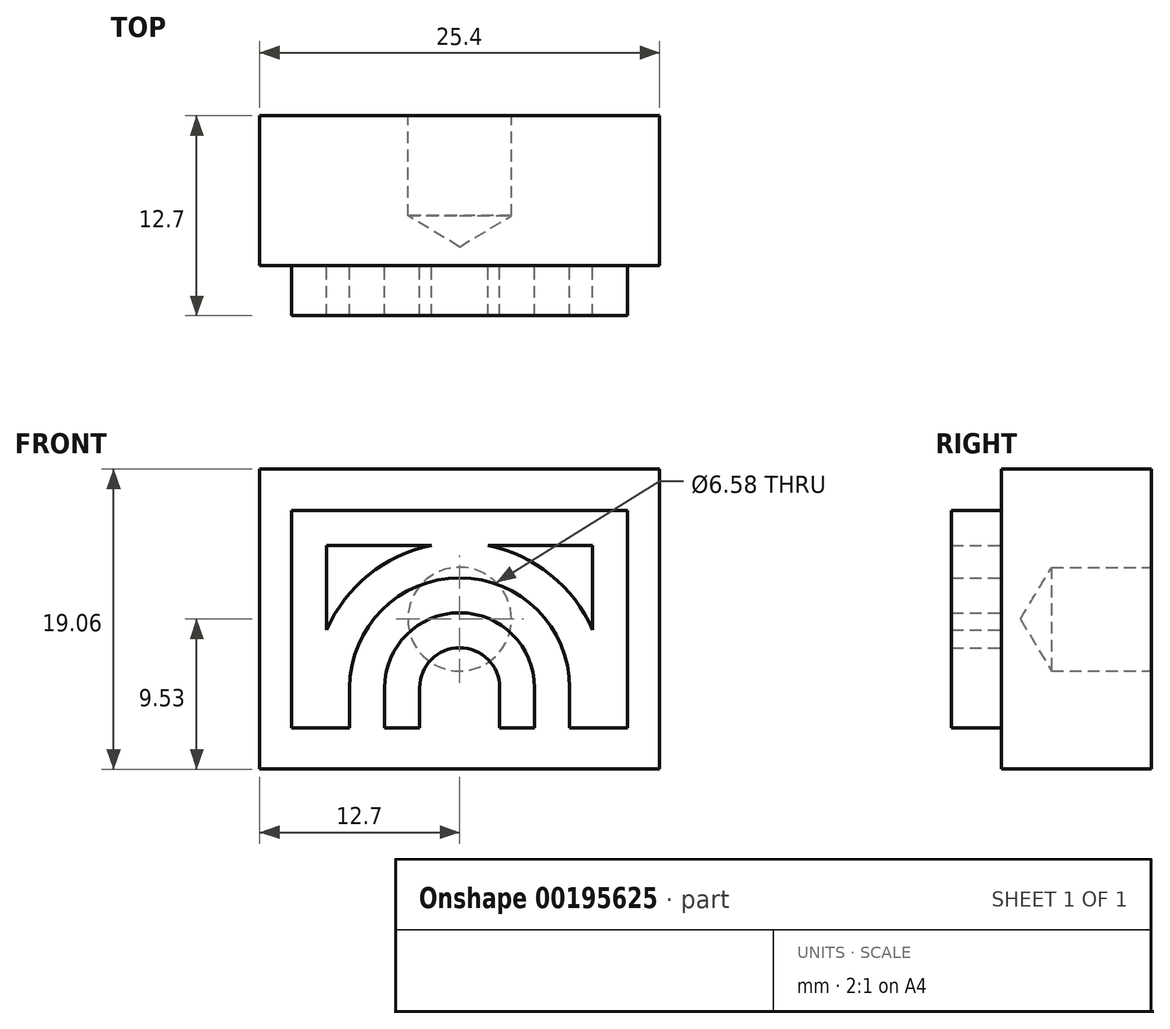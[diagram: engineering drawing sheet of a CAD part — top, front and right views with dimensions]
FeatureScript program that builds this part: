
annotation { "Feature Type Name" : "Feature", "Feature Type Description" : "" }
export const myFeature = defineFeature(function(context is Context, id is Id, definition is map)
    precondition{}
    {
        {
            var Q0;
            Q0=qCreatedBy(makeId("Front.planeOp"),FACE);
            var sketch = newSketch(context, id + "F0", { "sketchPlane" : qUnion([Q0])});
            skLineSegment(sketch, "E0", {"start": v(0, 0) * mm, "end": v(0, 23.02) * mm, "construction": true});
            skLineSegment(sketch, "E1", {"start": v(0, 0) * mm, "end": v(0, -23.52) * mm, "construction": true});
            skLineSegment(sketch, "E2", {"start": v(-25.56, 0) * mm, "end": v(25.9, 0) * mm, "construction": true});
            skLineSegment(sketch, "E3.bottom", {"start": v(-12.7, 9.53) * mm, "end": v(12.7, 9.52) * mm});
            skLineSegment(sketch, "E3.top", {"start": v(-12.7, -9.53) * mm, "end": v(12.7, -9.53) * mm});
            skLineSegment(sketch, "E3.left", {"start": v(-12.7, 9.53) * mm, "end": v(-12.7, -9.53) * mm});
            skLineSegment(sketch, "E3.right", {"start": v(12.7, 9.53) * mm, "end": v(12.7, -9.53) * mm});
            skSolve(sketch);
        }
        {
            var Q0;
            Q0 = qSketchRegion(id + "F0", true);
            extrude(context, id + "F1", {"entities" : qUnion([Q0]), "oppositeDirection" : true, "depth" : 9.52 * mm});
        }
        {
            var Q0;
            Q0=makeQuery(id+"F1.opExtrude","CAP_FACE",FACE,{"disambiguationData":[OSD([sQuery(id+"F0.wireOp",EDGE,"E3.bottom"),sQuery(id+"F0.wireOp",EDGE,"E3.top"),sQuery(id+"F0.wireOp",EDGE,"E3.left"),sQuery(id+"F0.wireOp",EDGE,"E3.right")])],"isStart":true});
            var sketch = newSketch(context, id + "F2", { "sketchPlane" : qUnion([Q0])});
            skLineSegment(sketch, "E4", {"start": v(0, 9) * mm, "end": v(0, -9.1) * mm, "construction": true});
            skLineSegment(sketch, "E5.MirrorCS", {"start": v(0, 6.9) * mm, "end": v(10.66, 6.9) * mm});
            skLineSegment(sketch, "E6.MirrorCS", {"start": v(2.54, -6.9) * mm, "end": v(4.76, -6.9) * mm});
            skLineSegment(sketch, "E7.MirrorCS", {"start": v(6.99, -6.9) * mm, "end": v(10.66, -6.9) * mm});
            skLineSegment(sketch, "E8.MirrorCS", {"start": v(2.54, -4.36) * mm, "end": v(2.54, -6.9) * mm});
            skLineSegment(sketch, "E9.MirrorCS", {"start": v(6.99, -4.36) * mm, "end": v(6.99, -6.9) * mm});
            skLineSegment(sketch, "E10.MirrorCS", {"start": v(10.66, -6.9) * mm, "end": v(10.66, 6.9) * mm});
            skLineSegment(sketch, "E11", {"start": v(1.8, 4.67) * mm, "end": v(8.44, 4.67) * mm});
            skLineSegment(sketch, "E12", {"start": v(8.44, 4.67) * mm, "end": v(8.44, -0.68) * mm});
            skLineSegment(sketch, "E13", {"start": v(4.76, -6.9) * mm, "end": v(4.76, -4.36) * mm});
            skLineSegment(sketch, "E14", {"start": v(10.66, -6.9) * mm, "end": v(0, -6.9) * mm, "construction": true});
            skLineSegment(sketch, "E15", {"start": v(0, -4.36) * mm, "end": v(10.66, -4.36) * mm, "construction": true});
            skArc(sketch, "E16", {"start": v(2.54, -4.36) * mm, "mid": v(1.8, -2.56) * mm, "end": v(0, -1.82) * mm});
            skArc(sketch, "E17", {"start": v(6.99, -4.36) * mm, "mid": v(4.94, 0.58) * mm, "end": v(0, 2.63) * mm});
            skArc(sketch, "E18", {"start": v(4.76, -4.36) * mm, "mid": v(3.37, -0.99) * mm, "end": v(0, 0.4) * mm});
            skArc(sketch, "E19", {"start": v(8.44, -0.68) * mm, "mid": v(5.78, 2.81) * mm, "end": v(1.8, 4.67) * mm});
            skLineSegment(sketch, "E20.MirrorCS", {"start": v(-6.98, -6.9) * mm, "end": v(-10.66, -6.9) * mm});
            skLineSegment(sketch, "E21.MirrorCS", {"start": v(-2.54, -6.9) * mm, "end": v(-4.76, -6.9) * mm});
            skArc(sketch, "E22.MirrorCS", {"start": v(-6.99, -4.36) * mm, "mid": v(-4.94, 0.58) * mm, "end": v(0, 2.63) * mm});
            skLineSegment(sketch, "E23.MirrorCS", {"start": v(0, 6.9) * mm, "end": v(-10.66, 6.9) * mm});
            skLineSegment(sketch, "E24.MirrorCS", {"start": v(-4.76, -6.9) * mm, "end": v(-4.76, -4.36) * mm});
            skArc(sketch, "E25.MirrorCS", {"start": v(-4.76, -4.36) * mm, "mid": v(-3.37, -0.99) * mm, "end": v(0, 0.4) * mm});
            skLineSegment(sketch, "E26.MirrorCS", {"start": v(-2.54, -4.36) * mm, "end": v(-2.54, -6.9) * mm});
            skArc(sketch, "E27.MirrorCS", {"start": v(-8.44, -0.68) * mm, "mid": v(-5.78, 2.81) * mm, "end": v(-1.8, 4.67) * mm});
            skArc(sketch, "E28.MirrorCS", {"start": v(-2.54, -4.36) * mm, "mid": v(-1.8, -2.56) * mm, "end": v(0, -1.82) * mm});
            skLineSegment(sketch, "E29.MirrorCS", {"start": v(-1.8, 4.67) * mm, "end": v(-8.44, 4.67) * mm});
            skLineSegment(sketch, "E30.MirrorCS", {"start": v(-10.66, -6.9) * mm, "end": v(-10.66, 6.9) * mm});
            skLineSegment(sketch, "E31.MirrorCS", {"start": v(-6.98, -4.36) * mm, "end": v(-6.98, -6.9) * mm});
            skLineSegment(sketch, "E32.MirrorCS", {"start": v(-8.44, 4.67) * mm, "end": v(-8.44, -0.68) * mm});
            skSolve(sketch);
        }
        {
            var Q0;
            Q0 = qSketchRegion(id + "F2", true);
            extrude(context, id + "F3", {"entities" : qUnion([Q0]), "operationType" : NewBodyOperationType.ADD, "depth" : 3.17 * mm});
        }
        {
            var Q0;
            Q0=makeQuery(id+"F1.opExtrude","CAP_FACE",FACE,{"disambiguationData":[OSD([sQuery(id+"F0.wireOp",EDGE,"E3.bottom"),sQuery(id+"F0.wireOp",EDGE,"E3.top"),sQuery(id+"F0.wireOp",EDGE,"E3.left"),sQuery(id+"F0.wireOp",EDGE,"E3.right")])],"isStart":false});
            var sketch = newSketch(context, id + "F4", { "sketchPlane" : qUnion([Q0])});
            skLineSegment(sketch, "E33", {"start": v(0, 9.53) * mm, "end": v(0, -9.53) * mm, "construction": true});
            skPoint(sketch, "E34", {"position": v(0, 0) * mm});
            skSolve(sketch);
        }
        {
            var Q0;
            Q0=sQuery(id+"F4.wireOp",VERTEX,"E34");
            var Q1;
            Q1=makeQuery(id+"F1.opExtrude","SWEPT_BODY",BODY,{"disambiguationData":[OSD([sQuery(id+"F0.wireOp",EDGE,"E3.bottom"),sQuery(id+"F0.wireOp",EDGE,"E3.top"),sQuery(id+"F0.wireOp",EDGE,"E3.left"),sQuery(id+"F0.wireOp",EDGE,"E3.right")])]});
            hole(context, id + "F5", {"style" : HoleStyle.SIMPLE, "endStyle" : HoleEndStyle.BLIND, "holeDiameter" : 6.58 * mm, "majorDiameter" : 6.35 * mm, "holeDepth" : 6.35 * mm, "tappedDepth" : 12.7 * mm, "tapClearance" : 3, "startFromSketch" : true, "locations" : qUnion([Q0]), "scope" : qUnion([Q1])});
        }
    });
